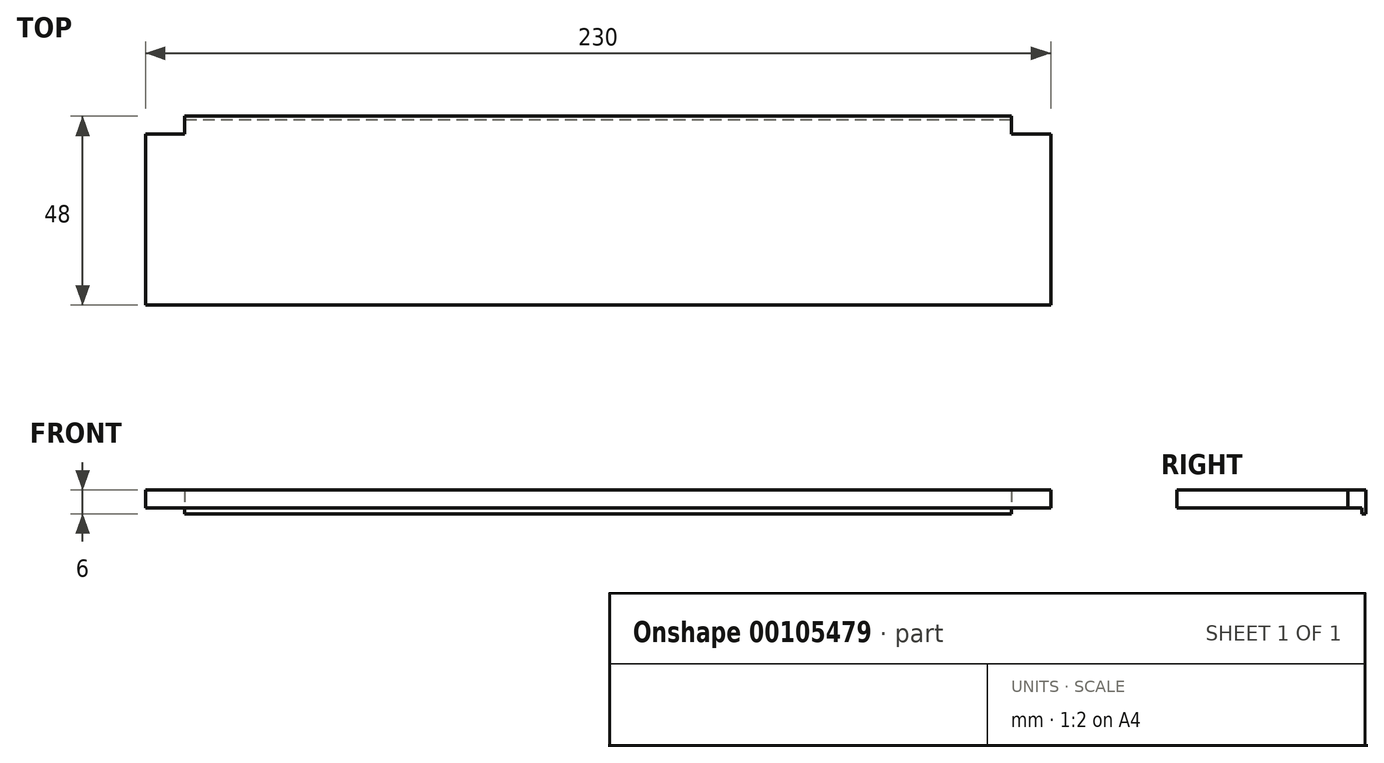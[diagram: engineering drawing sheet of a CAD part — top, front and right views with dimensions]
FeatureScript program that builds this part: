
annotation { "Feature Type Name" : "Feature", "Feature Type Description" : "" }
export const myFeature = defineFeature(function(context is Context, id is Id, definition is map)
    precondition{}
    {
        {
            var Q0;
            Q0=qCreatedBy(makeId("Top.planeOp"),FACE);
            var sketch = newSketch(context, id + "F0", { "sketchPlane" : qUnion([Q0])});
            skLineSegment(sketch, "E0.bottom", {"start": v(115, -24) * mm, "end": v(-115, -24) * mm});
            skLineSegment(sketch, "E0.top", {"start": v(115, 24) * mm, "end": v(-115, 24) * mm});
            skLineSegment(sketch, "E0.left", {"start": v(115, -24) * mm, "end": v(115, 24) * mm});
            skLineSegment(sketch, "E0.right", {"start": v(-115, -24) * mm, "end": v(-115, 24) * mm});
            skPoint(sketch, "E0.middle", {"position": v(0, 0) * mm});
            skLineSegment(sketch, "E1.bottom", {"start": v(-115, 24) * mm, "end": v(-105, 24) * mm});
            skLineSegment(sketch, "E1.top", {"start": v(-115, 19.5) * mm, "end": v(-105, 19.5) * mm});
            skLineSegment(sketch, "E1.left", {"start": v(-115, 24) * mm, "end": v(-115, 19.5) * mm});
            skLineSegment(sketch, "E1.right", {"start": v(-105, 24) * mm, "end": v(-105, 19.5) * mm});
            skLineSegment(sketch, "E2.bottom", {"start": v(115, 24) * mm, "end": v(105, 24) * mm});
            skLineSegment(sketch, "E2.top", {"start": v(115, 19.5) * mm, "end": v(105, 19.5) * mm});
            skLineSegment(sketch, "E2.left", {"start": v(115, 24) * mm, "end": v(115, 19.5) * mm});
            skLineSegment(sketch, "E2.right", {"start": v(105, 24) * mm, "end": v(105, 19.5) * mm});
            skSolve(sketch);
        }
        {
            var Q0;
            Q0=makeQuery(id+"F0.imprint","IMPRINT",FACE,{"disambiguationData":[TD([[makeQuery(id+"F0.imprint","IMPRINT",EDGE,{"derivedFrom":sQuery(id+"F0.wireOp",EDGE,"E0.bottom")}),-1.0]])]});
            extrude(context, id + "F1", {"entities" : qUnion([Q0]), "depth" : 4.5 * mm});
        }
        {
            var Q0;
            Q0=makeQuery(id+"F1.opExtrude","CAP_FACE",FACE,{"disambiguationData":[OSD([sQuery(id+"F0.wireOp",EDGE,"E0.bottom"),sQuery(id+"F0.wireOp",EDGE,"E0.top"),sQuery(id+"F0.wireOp",EDGE,"E0.left"),sQuery(id+"F0.wireOp",EDGE,"E0.right"),sQuery(id+"F0.wireOp",EDGE,"E1.top"),sQuery(id+"F0.wireOp",EDGE,"E1.right"),sQuery(id+"F0.wireOp",EDGE,"E2.top"),sQuery(id+"F0.wireOp",EDGE,"E2.right")])],"isStart":true});
            var sketch = newSketch(context, id + "F2", { "sketchPlane" : qUnion([Q0])});
            skLineSegment(sketch, "E3.bottom", {"start": v(105, -24) * mm, "end": v(-105, -24) * mm});
            skLineSegment(sketch, "E3.top", {"start": v(105, -23) * mm, "end": v(-105, -23) * mm});
            skLineSegment(sketch, "E3.left", {"start": v(105, -24) * mm, "end": v(105, -23) * mm});
            skLineSegment(sketch, "E3.right", {"start": v(-105, -24) * mm, "end": v(-105, -23) * mm});
            skSolve(sketch);
        }
        {
            var Q0;
            Q0 = qSketchRegion(id + "F2", true);
            extrude(context, id + "F3", {"entities" : qUnion([Q0]), "operationType" : NewBodyOperationType.ADD, "depth" : 1.5 * mm});
        }
    });
